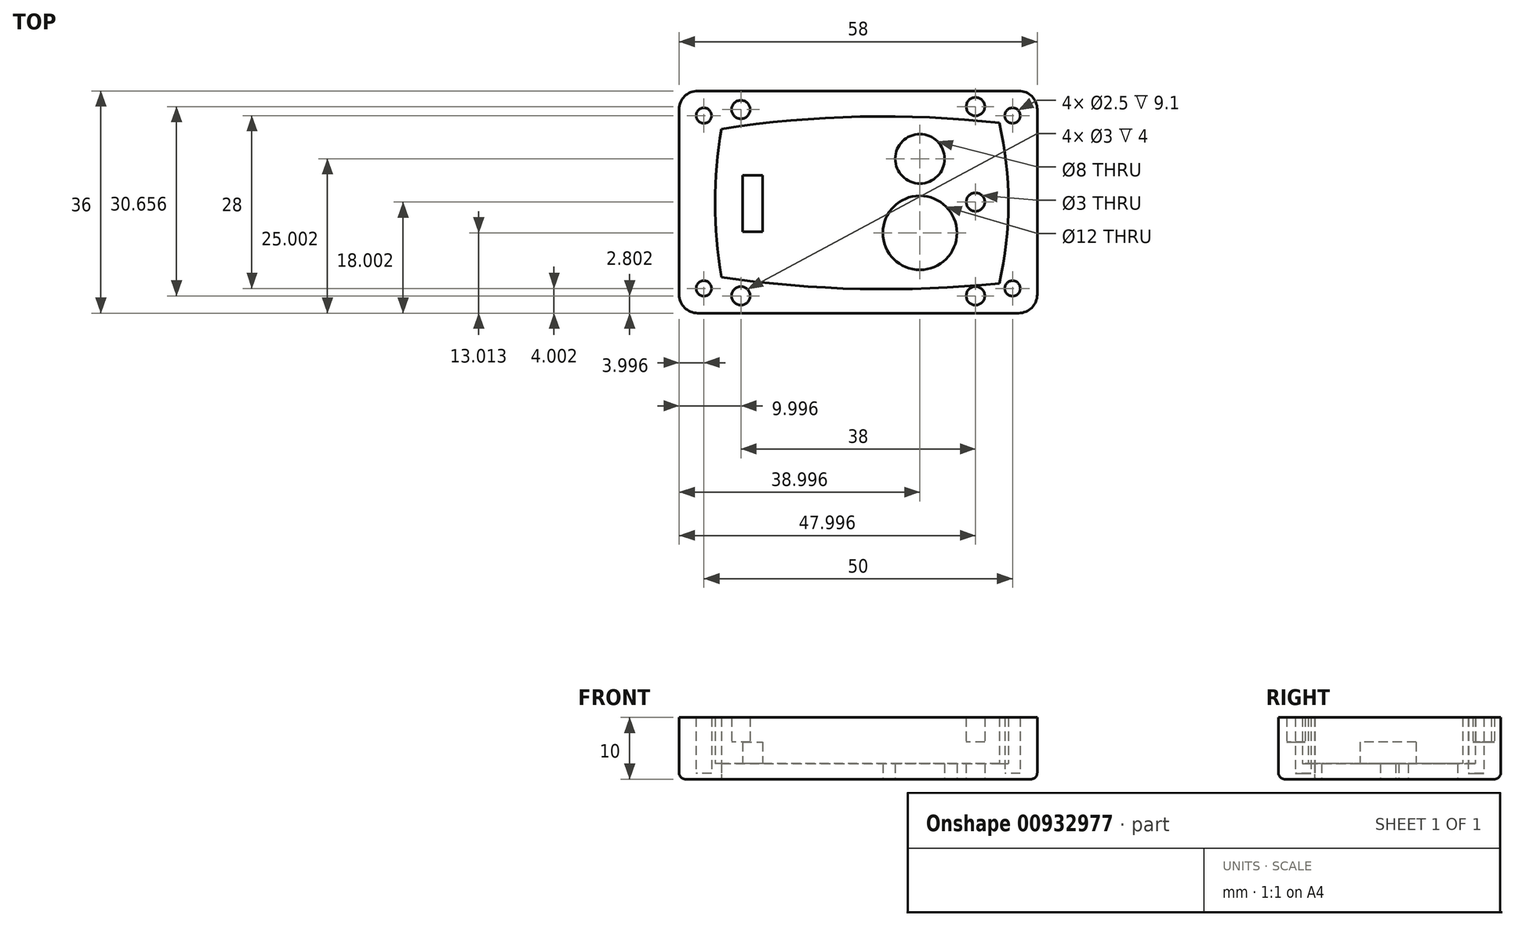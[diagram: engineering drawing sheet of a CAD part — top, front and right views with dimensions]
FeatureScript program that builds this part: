
annotation { "Feature Type Name" : "Feature", "Feature Type Description" : "" }
export const myFeature = defineFeature(function(context is Context, id is Id, definition is map)
    precondition{}
    {
        {
            var Q0;
            Q0=qCreatedBy(makeId("Top.planeOp"),FACE);
            var sketch = newSketch(context, id + "F0", { "sketchPlane" : qUnion([Q0])});
            skLineSegment(sketch, "E0", {"start": v(-0.01, 0.02) * mm, "end": v(-0.01, 24.02) * mm});
            skLineSegment(sketch, "E1", {"start": v(44.98, -1) * mm, "end": v(44.98, 25) * mm});
            skLineSegment(sketch, "E2", {"start": v(-0.01, 24.02) * mm, "end": v(44.98, 25) * mm});
            skLineSegment(sketch, "E3", {"start": v(-0.01, 0.02) * mm, "end": v(44.98, -1) * mm});
            skArc(sketch, "E4", {"start": v(44.98, 25) * mm, "mid": v(22.45, 26.01) * mm, "end": v(-0.01, 24.02) * mm});
            skArc(sketch, "E5", {"start": v(0, 0) * mm, "mid": v(22.46, -1.9) * mm, "end": v(44.98, -1) * mm});
            skArc(sketch, "E6", {"start": v(44.98, -1) * mm, "mid": v(46.47, 12) * mm, "end": v(44.98, 25) * mm});
            skArc(sketch, "E7", {"start": v(-0.01, 24.02) * mm, "mid": v(-1.07, 12.01) * mm, "end": v(0, 0) * mm});
            skCircle(sketch, "E8", {"center": v(2.96, 21.67) * mm, "radius": 1 * mm});
            skCircle(sketch, "E9", {"center": v(2.96, 2.08) * mm, "radius": 1 * mm});
            skCircle(sketch, "E10", {"center": v(41.71, 2.08) * mm, "radius": 1 * mm});
            skCircle(sketch, "E11", {"center": v(41.71, 21.67) * mm, "radius": 1 * mm});
            skLineSegment(sketch, "E12.bottom", {"start": v(-6.87, 30.18) * mm, "end": v(51.13, 30.18) * mm});
            skLineSegment(sketch, "E12.top", {"start": v(-6.87, -5.82) * mm, "end": v(51.13, -5.82) * mm});
            skLineSegment(sketch, "E12.left", {"start": v(-6.87, 30.18) * mm, "end": v(-6.87, -5.82) * mm});
            skLineSegment(sketch, "E12.right", {"start": v(51.13, 30.18) * mm, "end": v(51.13, -5.82) * mm});
            skCircle(sketch, "E13", {"center": v(-2.87, 26.18) * mm, "radius": 1.25 * mm});
            skCircle(sketch, "E14", {"center": v(-2.87, -1.82) * mm, "radius": 1.25 * mm});
            skCircle(sketch, "E15", {"center": v(47.13, 26.18) * mm, "radius": 1.25 * mm});
            skCircle(sketch, "E16", {"center": v(47.13, -1.82) * mm, "radius": 1.25 * mm});
            skCircle(sketch, "E17", {"center": v(18.8, 12.3) * mm, "radius": 1 * mm});
            skCircle(sketch, "E18", {"center": v(26.8, 12.3) * mm, "radius": 1 * mm});
            skLineSegment(sketch, "E19.bottom", {"start": v(3.37, 16.48) * mm, "end": v(6.66, 16.48) * mm});
            skLineSegment(sketch, "E19.top", {"start": v(3.37, 7.4) * mm, "end": v(6.66, 7.4) * mm});
            skLineSegment(sketch, "E19.left", {"start": v(3.37, 16.48) * mm, "end": v(3.37, 7.4) * mm});
            skLineSegment(sketch, "E19.right", {"start": v(6.66, 16.48) * mm, "end": v(6.66, 7.4) * mm});
            skLineSegment(sketch, "E20.bottom", {"start": v(26.13, 9.18) * mm, "end": v(38.13, 9.18) * mm});
            skLineSegment(sketch, "E20.top", {"start": v(26.13, 1.18) * mm, "end": v(38.13, 1.18) * mm});
            skLineSegment(sketch, "E20.left", {"start": v(26.13, 9.18) * mm, "end": v(26.13, 1.18) * mm});
            skLineSegment(sketch, "E20.right", {"start": v(38.13, 9.18) * mm, "end": v(38.13, 1.18) * mm});
            skCircle(sketch, "E21", {"center": v(32.13, 7.2) * mm, "radius": 6 * mm});
            skPoint(sketch, "E22", {"position": v(32.13, 9.18) * mm});
            skCircle(sketch, "E23", {"center": v(3.13, 27.16) * mm, "radius": 1.5 * mm});
            skCircle(sketch, "E24", {"center": v(41.13, 27.64) * mm, "radius": 1.5 * mm});
            skCircle(sketch, "E25", {"center": v(3.13, -3.02) * mm, "radius": 1.5 * mm});
            skCircle(sketch, "E26", {"center": v(41.13, -3.02) * mm, "radius": 1.5 * mm});
            skCircle(sketch, "E27", {"center": v(41.13, 12.18) * mm, "radius": 1.5 * mm});
            skCircle(sketch, "E28", {"center": v(32.13, 19.18) * mm, "radius": 4 * mm});
            skSolve(sketch);
        }
        {
            var Q0;
            {var subQ1=sQuery(id+"F0.wireOp",EDGE,"E4");Q0=makeQuery(id+"F0.imprint","IMPRINT",FACE,{"disambiguationData":[TD([[makeQuery(id+"F0.imprint","IMPRINT",EDGE,{"derivedFrom":subQ1}),-1.0]])]});}
            var Q1;
            Q1=makeQuery(id+"F0.imprint","IMPRINT",FACE,{"disambiguationData":[TD([[makeQuery(id+"F0.imprint","IMPRINT",EDGE,{"derivedFrom":sQuery(id+"F0.wireOp",EDGE,"E13")}),1.0]])]});
            var Q2;
            Q2=makeQuery(id+"F0.imprint","IMPRINT",FACE,{"disambiguationData":[TD([[makeQuery(id+"F0.imprint","IMPRINT",EDGE,{"derivedFrom":sQuery(id+"F0.wireOp",EDGE,"E15")}),1.0]])]});
            var Q3;
            Q3=makeQuery(id+"F0.imprint","IMPRINT",FACE,{"disambiguationData":[TD([[makeQuery(id+"F0.imprint","IMPRINT",EDGE,{"derivedFrom":sQuery(id+"F0.wireOp",EDGE,"E16")}),1.0]])]});
            var Q4;
            Q4=makeQuery(id+"F0.imprint","IMPRINT",FACE,{"disambiguationData":[TD([[makeQuery(id+"F0.imprint","IMPRINT",EDGE,{"derivedFrom":sQuery(id+"F0.wireOp",EDGE,"E14")}),1.0]])]});
            var Q5;
            Q5=makeQuery(id+"F0.imprint","IMPRINT",FACE,{"disambiguationData":[TD([[makeQuery(id+"F0.imprint","IMPRINT",EDGE,{"derivedFrom":sQuery(id+"F0.wireOp",EDGE,"E25")}),1.0]])]});
            var Q6;
            Q6=makeQuery(id+"F0.imprint","IMPRINT",FACE,{"disambiguationData":[TD([[makeQuery(id+"F0.imprint","IMPRINT",EDGE,{"derivedFrom":sQuery(id+"F0.wireOp",EDGE,"E23")}),1.0]])]});
            var Q7;
            Q7=makeQuery(id+"F0.imprint","IMPRINT",FACE,{"disambiguationData":[TD([[makeQuery(id+"F0.imprint","IMPRINT",EDGE,{"derivedFrom":sQuery(id+"F0.wireOp",EDGE,"E24")}),1.0]])]});
            var Q8;
            Q8=makeQuery(id+"F0.imprint","IMPRINT",FACE,{"disambiguationData":[TD([[makeQuery(id+"F0.imprint","IMPRINT",EDGE,{"derivedFrom":sQuery(id+"F0.wireOp",EDGE,"E26")}),1.0]])]});
            extrude(context, id + "F1", {"entities" : qUnion([Q0, Q1, Q2, Q3, Q4, Q5, Q6, Q7, Q8]), "depth" : 10 * mm, "offsetDistance" : 25 * mm});
        }
        {
            var Q0;
            {var subQ1=sQuery(id+"F0.wireOp",EDGE,"E1");Q0=makeQuery(id+"F0.imprint","IMPRINT",FACE,{"disambiguationData":[TD([[makeQuery(id+"F0.imprint","IMPRINT",EDGE,{"derivedFrom":subQ1}),1.0]])]});}
            var Q1;
            Q1=makeQuery(id+"F0.imprint","IMPRINT",FACE,{"disambiguationData":[TD([[makeQuery(id+"F0.imprint","IMPRINT",EDGE,{"derivedFrom":sQuery(id+"F0.wireOp",EDGE,"E8")}),1.0]])]});
            var Q2;
            Q2=makeQuery(id+"F0.imprint","IMPRINT",FACE,{"disambiguationData":[TD([[makeQuery(id+"F0.imprint","IMPRINT",EDGE,{"derivedFrom":sQuery(id+"F0.wireOp",EDGE,"E9")}),1.0]])]});
            var Q3;
            Q3=makeQuery(id+"F0.imprint","IMPRINT",FACE,{"disambiguationData":[TD([[makeQuery(id+"F0.imprint","IMPRINT",EDGE,{"derivedFrom":sQuery(id+"F0.wireOp",EDGE,"E10")}),1.0]])]});
            var Q4;
            Q4=makeQuery(id+"F0.imprint","IMPRINT",FACE,{"disambiguationData":[TD([[makeQuery(id+"F0.imprint","IMPRINT",EDGE,{"derivedFrom":sQuery(id+"F0.wireOp",EDGE,"E11")}),1.0]])]});
            var Q5;
            Q5=makeQuery(id+"F0.imprint","IMPRINT",FACE,{"disambiguationData":[TD([[makeQuery(id+"F0.imprint","IMPRINT",EDGE,{"derivedFrom":sQuery(id+"F0.wireOp",EDGE,"E2")}),1.0]])]});
            var Q6;
            {var subQ0=sQuery(id+"F0.wireOp",EDGE,"E5");Q6=makeQuery(id+"F0.imprint","IMPRINT",FACE,{"disambiguationData":[TD([[makeQuery(id+"F0.imprint","IMPRINT",EDGE,{"derivedFrom":subQ0}),1.0]])]});}
            var Q7;
            Q7=makeQuery(id+"F0.imprint","IMPRINT",FACE,{"disambiguationData":[TD([[makeQuery(id+"F0.imprint","IMPRINT",EDGE,{"derivedFrom":sQuery(id+"F0.wireOp",EDGE,"E1")}),-1.0]])]});
            var Q8;
            {var subQ0=sQuery(id+"F0.wireOp",EDGE,"E7");var subQ1=sQuery(id+"F0.wireOp",EDGE,"E0");var subQ3=makeQuery(id+"F0.imprint","INTERSECT",VERTEX,{"derivedFrom":[subQ1,subQ0]});Q8=makeQuery(id+"F0.imprint","IMPRINT",FACE,{"disambiguationData":[TD([[makeQuery(id+"F0.imprint","IMPRINT",EDGE,{"disambiguationData":[TD([[subQ3,-1.0]])],"derivedFrom":subQ1}),1.0]])]});}
            var Q9;
            Q9=makeQuery(id+"F0.imprint","IMPRINT",FACE,{"disambiguationData":[TD([[makeQuery(id+"F0.imprint","IMPRINT",EDGE,{"derivedFrom":sQuery(id+"F0.wireOp",EDGE,"E19.bottom")}),-1.0]])]});
            var Q10;
            Q10=makeQuery(id+"F0.imprint","IMPRINT",FACE,{"disambiguationData":[TD([[makeQuery(id+"F0.imprint","IMPRINT",EDGE,{"derivedFrom":sQuery(id+"F0.wireOp",EDGE,"E17")}),1.0]])]});
            var Q11;
            Q11=makeQuery(id+"F0.imprint","IMPRINT",FACE,{"disambiguationData":[TD([[makeQuery(id+"F0.imprint","IMPRINT",EDGE,{"derivedFrom":sQuery(id+"F0.wireOp",EDGE,"E18")}),1.0]])]});
            var Q12;
            Q12=makeQuery(id+"F0.imprint","IMPRINT",FACE,{"disambiguationData":[TD([[makeQuery(id+"F0.imprint","IMPRINT",EDGE,{"derivedFrom":sQuery(id+"F0.wireOp",EDGE,"E20.bottom")}),-1.0]])]});
            var Q13;
            {var subQ0=sQuery(id+"F0.wireOp",EDGE,"E20.right");var subQ1=sQuery(id+"F0.wireOp",EDGE,"E20.top");var subQ2=makeQuery(id+"F0.imprint","INTERSECT",VERTEX,{"derivedFrom":[subQ1,subQ0]});Q13=makeQuery(id+"F0.imprint","IMPRINT",FACE,{"disambiguationData":[TD([[makeQuery(id+"F0.imprint","IMPRINT",EDGE,{"disambiguationData":[TD([[subQ2,1.0]])],"derivedFrom":subQ1}),1.0]])]});}
            extrude(context, id + "F2", {"entities" : qUnion([Q0, Q1, Q2, Q3, Q4, Q5, Q6, Q7, Q8, Q9, Q10, Q11, Q12, Q13]), "operationType" : NewBodyOperationType.ADD, "depth" : 2.5 * mm, "offsetDistance" : 25 * mm});
        }
        {
            var Q0;
            Q0=makeQuery(id+"F1.opExtrude","SWEPT_EDGE",EDGE,{"disambiguationData":[OSD([sQuery(id+"F0.wireOp",EDGE,"E12.bottom"),sQuery(id+"F0.wireOp",EDGE,"E12.right")])]});
            var Q1;
            Q1=makeQuery(id+"F1.opExtrude","SWEPT_EDGE",EDGE,{"disambiguationData":[OSD([sQuery(id+"F0.wireOp",EDGE,"E12.top"),sQuery(id+"F0.wireOp",EDGE,"E12.right")])]});
            var Q2;
            Q2=makeQuery(id+"F1.opExtrude","SWEPT_EDGE",EDGE,{"disambiguationData":[OSD([sQuery(id+"F0.wireOp",EDGE,"E12.top"),sQuery(id+"F0.wireOp",EDGE,"E12.left")])]});
            var Q3;
            Q3=makeQuery(id+"F1.opExtrude","SWEPT_EDGE",EDGE,{"disambiguationData":[OSD([sQuery(id+"F0.wireOp",EDGE,"E12.bottom"),sQuery(id+"F0.wireOp",EDGE,"E12.left")])]});
            fillet(context, id + "F3", {"entities" : qUnion([Q0, Q1, Q2, Q3]), "radius" : 3 * mm, "tangentPropagation" : true, "allowEdgeOverflow" : false});
        }
        {
            var Q0;
            Q0=makeQuery(id+"F0.imprint","IMPRINT",FACE,{"disambiguationData":[TD([[makeQuery(id+"F0.imprint","IMPRINT",EDGE,{"derivedFrom":sQuery(id+"F0.wireOp",EDGE,"E19.bottom")}),-1.0]])]});
            extrude(context, id + "F4", {"entities" : qUnion([Q0]), "operationType" : NewBodyOperationType.ADD, "depth" : 6 * mm, "offsetDistance" : 25 * mm});
        }
        {
            var Q0;
            Q0=makeQuery(id+"F0.imprint","IMPRINT",FACE,{"disambiguationData":[TD([[makeQuery(id+"F0.imprint","IMPRINT",EDGE,{"derivedFrom":sQuery(id+"F0.wireOp",EDGE,"E15")}),1.0]])]});
            var Q1;
            Q1=makeQuery(id+"F0.imprint","IMPRINT",FACE,{"disambiguationData":[TD([[makeQuery(id+"F0.imprint","IMPRINT",EDGE,{"derivedFrom":sQuery(id+"F0.wireOp",EDGE,"E13")}),1.0]])]});
            var Q2;
            Q2=makeQuery(id+"F0.imprint","IMPRINT",FACE,{"disambiguationData":[TD([[makeQuery(id+"F0.imprint","IMPRINT",EDGE,{"derivedFrom":sQuery(id+"F0.wireOp",EDGE,"E14")}),1.0]])]});
            var Q3;
            Q3=makeQuery(id+"F0.imprint","IMPRINT",FACE,{"disambiguationData":[TD([[makeQuery(id+"F0.imprint","IMPRINT",EDGE,{"derivedFrom":sQuery(id+"F0.wireOp",EDGE,"E16")}),1.0]])]});
            extrude(context, id + "F5", {"entities" : qUnion([Q0, Q1, Q2, Q3]), "operationType" : NewBodyOperationType.REMOVE, "depth" : 17.1 * mm, "offsetDistance" : 25 * mm, "hasSecondDirection" : true, "secondDirectionOppositeDirection" : false, "secondDirectionDepth" : 0.9 * mm});
        }
        {
            var Q0;
            Q0=makeQuery(id+"F0.imprint","IMPRINT",FACE,{"disambiguationData":[TD([[makeQuery(id+"F0.imprint","IMPRINT",EDGE,{"derivedFrom":sQuery(id+"F0.wireOp",EDGE,"E23")}),1.0]])]});
            var Q1;
            Q1=makeQuery(id+"F0.imprint","IMPRINT",FACE,{"disambiguationData":[TD([[makeQuery(id+"F0.imprint","IMPRINT",EDGE,{"derivedFrom":sQuery(id+"F0.wireOp",EDGE,"E24")}),1.0]])]});
            var Q2;
            Q2=makeQuery(id+"F0.imprint","IMPRINT",FACE,{"disambiguationData":[TD([[makeQuery(id+"F0.imprint","IMPRINT",EDGE,{"derivedFrom":sQuery(id+"F0.wireOp",EDGE,"E26")}),1.0]])]});
            var Q3;
            Q3=makeQuery(id+"F0.imprint","IMPRINT",FACE,{"disambiguationData":[TD([[makeQuery(id+"F0.imprint","IMPRINT",EDGE,{"derivedFrom":sQuery(id+"F0.wireOp",EDGE,"E25")}),1.0]])]});
            extrude(context, id + "F6", {"entities" : qUnion([Q0, Q1, Q2, Q3]), "operationType" : NewBodyOperationType.REMOVE, "depth" : 16.7 * mm, "offsetDistance" : 25 * mm, "hasSecondDirection" : true, "secondDirectionOppositeDirection" : false, "secondDirectionDepth" : 6 * mm});
        }
        {
            var Q0;
            Q0=makeQuery(id+"F1.opExtrude","CAP_EDGE",EDGE,{"disambiguationData":[OSD([sQuery(id+"F0.wireOp",EDGE,"E12.right")])],"isStart":true});
            fillet(context, id + "F7", {"entities" : qUnion([Q0]), "radius" : 1 * mm, "tangentPropagation" : true, "allowEdgeOverflow" : false});
        }
    });
